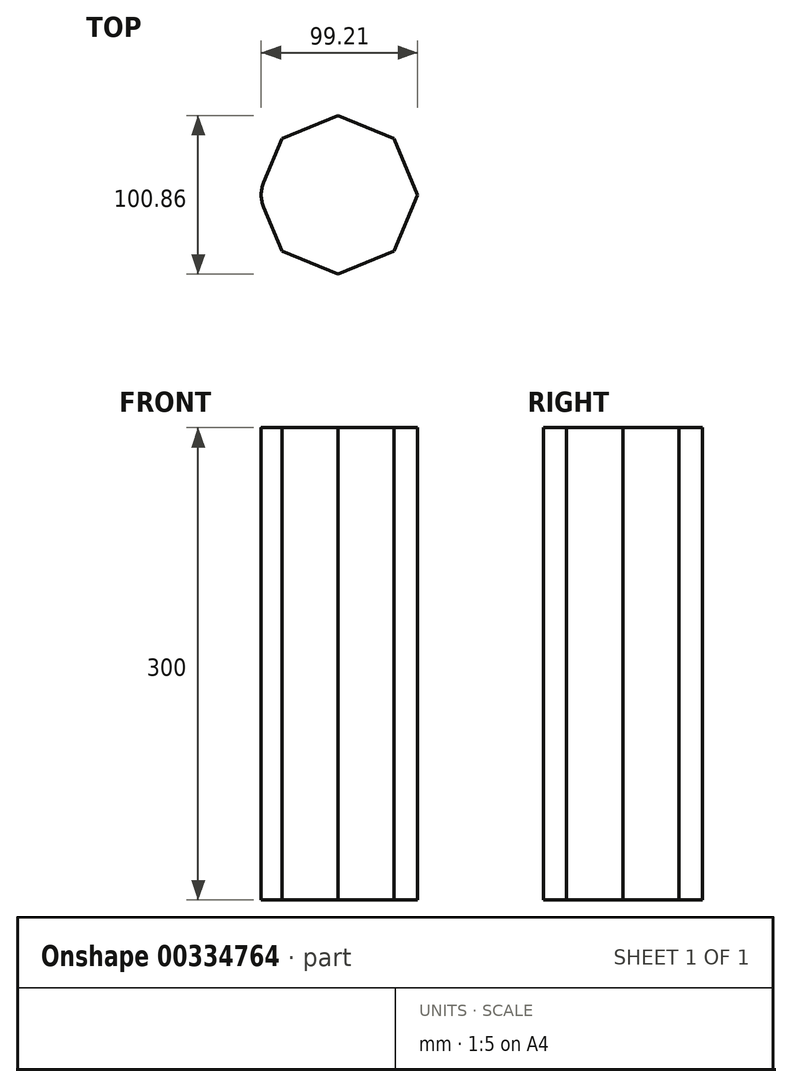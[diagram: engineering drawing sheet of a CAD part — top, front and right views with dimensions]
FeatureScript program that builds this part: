
annotation { "Feature Type Name" : "Feature", "Feature Type Description" : "" }
export const myFeature = defineFeature(function(context is Context, id is Id, definition is map)
    precondition{}
    {
        {
            var Q0;
            Q0=qCreatedBy(makeId("Top.planeOp"),FACE);
            var sketch = newSketch(context, id + "F0", { "sketchPlane" : qUnion([Q0])});
            skCircle(sketch, "E0.cCircle", {"center": v(0, 0) * mm, "radius": 50.43 * mm, "construction": true});
            skLineSegment(sketch, "E0.0", {"start": v(0, 50.43) * mm, "end": v(35.66, 35.66) * mm});
            skLineSegment(sketch, "E0.1", {"start": v(35.66, 35.66) * mm, "end": v(50.43, 0) * mm});
            skLineSegment(sketch, "E0.2", {"start": v(50.43, 0) * mm, "end": v(35.66, -35.66) * mm});
            skLineSegment(sketch, "E0.3", {"start": v(35.66, -35.66) * mm, "end": v(0, -50.43) * mm});
            skLineSegment(sketch, "E0.4", {"start": v(0, -50.43) * mm, "end": v(-35.66, -35.66) * mm});
            skLineSegment(sketch, "E0.5", {"start": v(-35.66, -35.66) * mm, "end": v(-50.43, 0) * mm});
            skLineSegment(sketch, "E0.6", {"start": v(-50.43, 0) * mm, "end": v(-35.66, 35.66) * mm});
            skLineSegment(sketch, "E0.7", {"start": v(-35.66, 35.66) * mm, "end": v(0, 50.43) * mm});
            skSolve(sketch);
        }
        {
            var Q0;
            Q0=makeQuery(id+"F0.imprint","IMPRINT",FACE,{"disambiguationData":[TD([[makeQuery(id+"F0.imprint","IMPRINT",EDGE,{"derivedFrom":sQuery(id+"F0.wireOp",EDGE,"E0.0")}),-1.0]])]});
            extrude(context, id + "F1", {"entities" : qUnion([Q0]), "depth" : 300 * mm});
        }
        {
            var Q0;
            Q0=makeQuery(id+"F1.opExtrude","SWEPT_EDGE",EDGE,{"disambiguationData":[OSD([sQuery(id+"F0.wireOp",EDGE,"E0.5"),sQuery(id+"F0.wireOp",EDGE,"E0.6")])]});
            fillet(context, id + "F2", {"entities" : qUnion([Q0]), "radius" : 20 * mm, "tangentPropagation" : true, "allowEdgeOverflow" : false});
        }
    });
